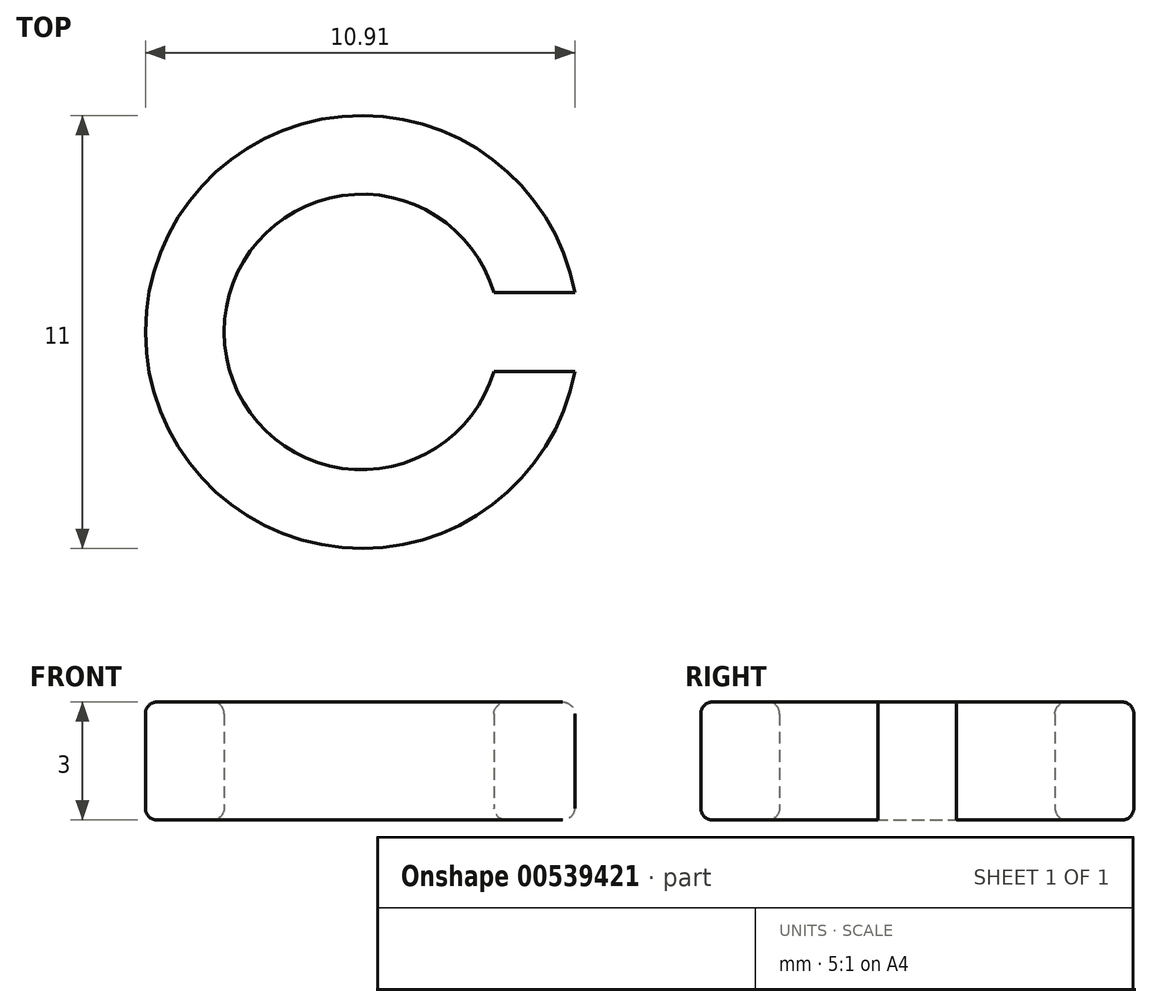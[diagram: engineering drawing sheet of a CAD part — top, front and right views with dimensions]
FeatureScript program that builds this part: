
annotation { "Feature Type Name" : "Feature", "Feature Type Description" : "" }
export const myFeature = defineFeature(function(context is Context, id is Id, definition is map)
    precondition{}
    {
        {
            var Q0;
            Q0=qCreatedBy(makeId("Front.planeOp"),FACE);
            var sketch = newSketch(context, id + "F0", { "sketchPlane" : qUnion([Q0])});
            skLineSegment(sketch, "E0.bottom", {"start": v(3.8, 0) * mm, "end": v(5.2, 0) * mm});
            skLineSegment(sketch, "E0.top", {"start": v(3.8, 3) * mm, "end": v(5.2, 3) * mm});
            skLineSegment(sketch, "E0.left", {"start": v(3.5, 0.3) * mm, "end": v(3.5, 2.7) * mm});
            skLineSegment(sketch, "E0.right", {"start": v(5.5, 0.3) * mm, "end": v(5.5, 2.7) * mm});
            skPoint(sketch, "E1.visualSharp", {"position": v(3.5, 3) * mm});
            skArc(sketch, "E1.filletArc", {"start": v(3.8, 3) * mm, "mid": v(3.59, 2.91) * mm, "end": v(3.5, 2.7) * mm});
            skPoint(sketch, "E2.visualSharp", {"position": v(3.5, 0) * mm});
            skArc(sketch, "E2.filletArc", {"start": v(3.5, 0.3) * mm, "mid": v(3.59, 0.09) * mm, "end": v(3.8, 0) * mm});
            skPoint(sketch, "E3.visualSharp", {"position": v(5.5, 3) * mm});
            skArc(sketch, "E3.filletArc", {"start": v(5.5, 2.7) * mm, "mid": v(5.41, 2.91) * mm, "end": v(5.2, 3) * mm});
            skPoint(sketch, "E4.visualSharp", {"position": v(5.5, 0) * mm});
            skArc(sketch, "E4.filletArc", {"start": v(5.2, 0) * mm, "mid": v(5.41, 0.09) * mm, "end": v(5.5, 0.3) * mm});
            skLineSegment(sketch, "E5", {"start": v(0, 0) * mm, "end": v(0, 7.7) * mm});
            skSolve(sketch);
        }
        {
            var Q0;
            Q0=makeQuery(id+"F0.imprint","IMPRINT",FACE,{"disambiguationData":[TD([[makeQuery(id+"F0.imprint","IMPRINT",EDGE,{"derivedFrom":sQuery(id+"F0.wireOp",EDGE,"E0.bottom")}),1.0]])]});
            var Q1;
            Q1=sQuery(id+"F0.wireOp",EDGE,"E5");
            revolve(context, id + "F1", {"entities" : qUnion([Q0]), "axis" : qUnion([Q1]), "revolveType" : RevolveType.FULL});
        }
        {
            var Q0;
            Q0=qCreatedBy(makeId("Top.planeOp"),FACE);
            var sketch = newSketch(context, id + "F2", { "sketchPlane" : qUnion([Q0])});
            skPoint(sketch, "E6", {"position": v(4.5, 0) * mm});
            skLineSegment(sketch, "E7.bottom", {"start": v(6.61, 1) * mm, "end": v(2.39, 1) * mm});
            skLineSegment(sketch, "E7.top", {"start": v(6.61, -1) * mm, "end": v(2.39, -1) * mm});
            skLineSegment(sketch, "E7.left", {"start": v(6.61, 1) * mm, "end": v(6.61, -1) * mm});
            skLineSegment(sketch, "E7.right", {"start": v(2.39, 1) * mm, "end": v(2.39, -1) * mm});
            skSolve(sketch);
        }
        {
            var Q0;
            Q0=makeQuery(id+"F2.imprint","IMPRINT",FACE,{"disambiguationData":[TD([[makeQuery(id+"F2.imprint","IMPRINT",EDGE,{"derivedFrom":sQuery(id+"F2.wireOp",EDGE,"E7.bottom")}),1.0]])]});
            extrude(context, id + "F3", {"entities" : qUnion([Q0]), "operationType" : NewBodyOperationType.REMOVE, "depth" : 4 * mm, "offsetDistance" : 25 * mm});
        }
    });
